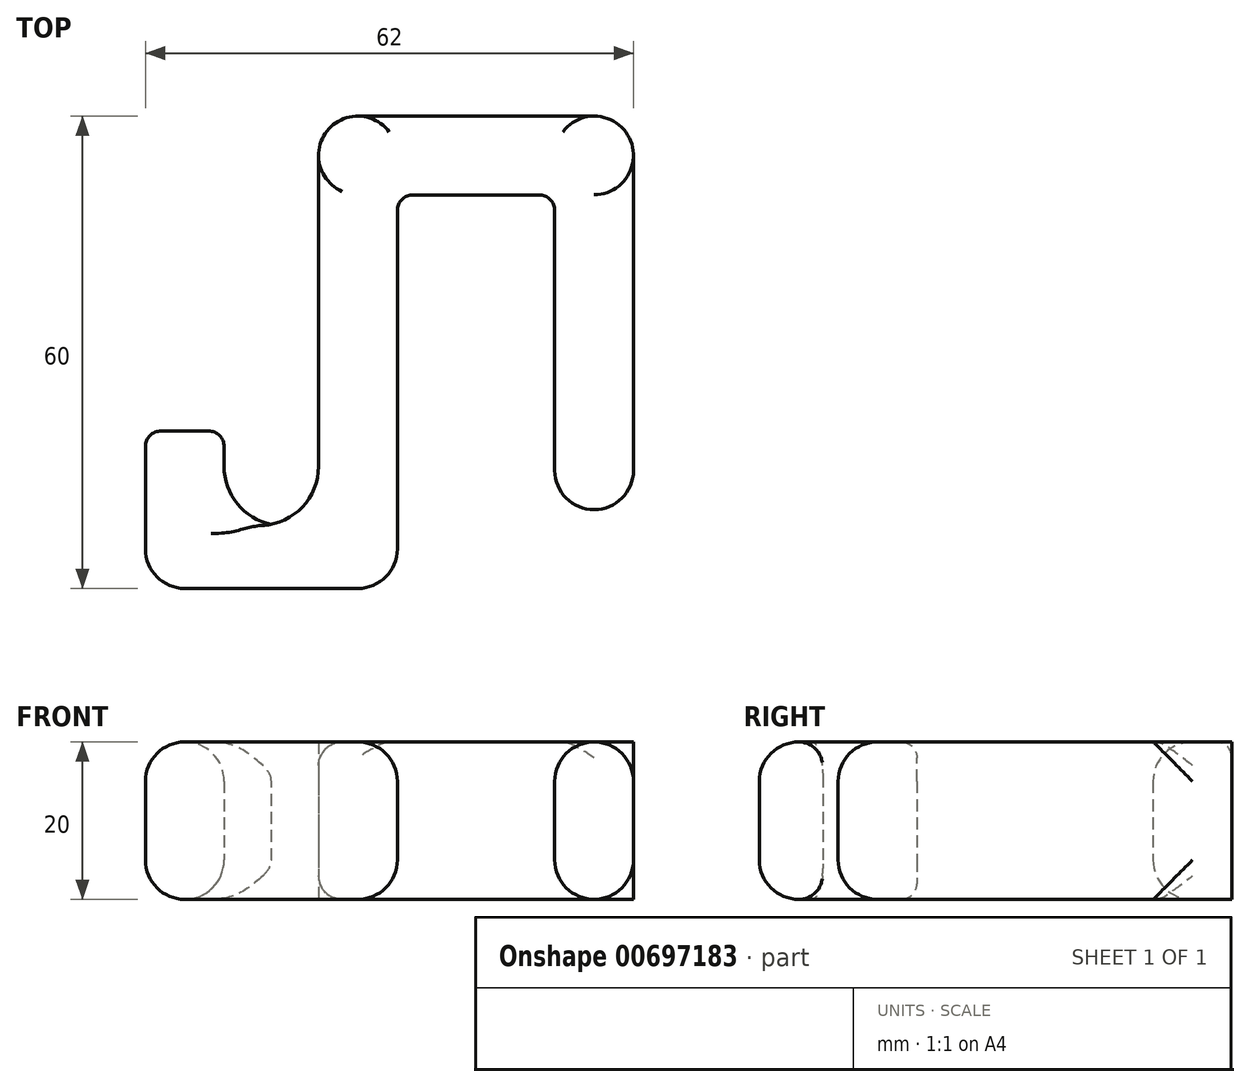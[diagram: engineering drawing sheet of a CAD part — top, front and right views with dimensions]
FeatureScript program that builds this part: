
annotation { "Feature Type Name" : "Feature", "Feature Type Description" : "" }
export const myFeature = defineFeature(function(context is Context, id is Id, definition is map)
    precondition{}
    {
        {
            var Q0;
            Q0=qCreatedBy(makeId("Top.planeOp"),FACE);
            var sketch = newSketch(context, id + "F0", { "sketchPlane" : qUnion([Q0])});
            skLineSegment(sketch, "E0.bottom", {"start": v(10, -20) * mm, "end": v(-10, -20) * mm});
            skLineSegment(sketch, "E0.top", {"start": v(10, 20) * mm, "end": v(-10, 20) * mm});
            skLineSegment(sketch, "E0.left", {"start": v(10, -20) * mm, "end": v(10, 20) * mm});
            skLineSegment(sketch, "E0.right", {"start": v(-10, -20) * mm, "end": v(-10, 20) * mm});
            skPoint(sketch, "E0.middle", {"position": v(0, 0) * mm});
            skLineSegment(sketch, "E1.0", {"start": v(-20, -20) * mm, "end": v(-20, 25) * mm});
            skLineSegment(sketch, "E1.1", {"start": v(15, 30) * mm, "end": v(-15, 30) * mm});
            skLineSegment(sketch, "E1.2", {"start": v(20, -20) * mm, "end": v(20, 25) * mm});
            skLineSegment(sketch, "E2", {"start": v(20, -20) * mm, "end": v(10, -20) * mm});
            skLineSegment(sketch, "E3", {"start": v(-10, -20) * mm, "end": v(-10, -30) * mm});
            skLineSegment(sketch, "E4", {"start": v(-10, -30) * mm, "end": v(-42, -30) * mm});
            skLineSegment(sketch, "E5", {"start": v(-42, -30) * mm, "end": v(-42, -10) * mm});
            skLineSegment(sketch, "E6", {"start": v(-42, -10) * mm, "end": v(-32, -10) * mm});
            skLineSegment(sketch, "E7", {"start": v(-32, -10) * mm, "end": v(-32, -22) * mm});
            skLineSegment(sketch, "E8", {"start": v(-32, -22) * mm, "end": v(-20, -22) * mm});
            skLineSegment(sketch, "E9", {"start": v(-20, -22) * mm, "end": v(-20, -20) * mm});
            skPoint(sketch, "E10.visualSharp", {"position": v(-20, 30) * mm});
            skArc(sketch, "E10.filletArc", {"start": v(-15, 30) * mm, "mid": v(-18.54, 28.54) * mm, "end": v(-20, 25) * mm});
            skPoint(sketch, "E11.visualSharp", {"position": v(20, 30) * mm});
            skArc(sketch, "E11.filletArc", {"start": v(20, 25) * mm, "mid": v(18.54, 28.54) * mm, "end": v(15, 30) * mm});
            skPoint(sketch, "E12.visualSharp", {"position": v(-42, -10) * mm});
            skLineSegment(sketch, "E12.filletArc", {"start": v(-42, -10) * mm, "end": v(-42, -10) * mm});
            skPoint(sketch, "E13.visualSharp", {"position": v(-32, -10) * mm});
            skLineSegment(sketch, "E13.filletArc", {"start": v(-32, -10) * mm, "end": v(-32, -10) * mm});
            skSolve(sketch);
        }
        {
            var Q0;
            Q0=makeQuery(id+"F0.imprint","IMPRINT",FACE,{"disambiguationData":[TD([[makeQuery(id+"F0.imprint","IMPRINT",EDGE,{"derivedFrom":sQuery(id+"F0.wireOp",EDGE,"E0.top")}),-1.0]])]});
            extrude(context, id + "F1", {"entities" : qUnion([Q0]), "depth" : 20 * mm, "offsetDistance" : 25 * mm});
        }
        {
            var Q0;
            Q0=makeQuery(id+"F1.opExtrude","SWEPT_EDGE",EDGE,{"disambiguationData":[OSD([sQuery(id+"F0.wireOp",EDGE,"E8"),sQuery(id+"F0.wireOp",EDGE,"E9")])]});
            var Q1;
            Q1=makeQuery(id+"F1.opExtrude","SWEPT_EDGE",EDGE,{"disambiguationData":[OSD([sQuery(id+"F0.wireOp",EDGE,"E7"),sQuery(id+"F0.wireOp",EDGE,"E8")])]});
            fillet(context, id + "F2", {"entities" : qUnion([Q0, Q1]), "radius" : 7.5 * mm, "tangentPropagation" : true, "allowEdgeOverflow" : false});
        }
        {
            var Q0;
            Q0=makeQuery(id+"F1.opExtrude","SWEPT_EDGE",EDGE,{"disambiguationData":[OSD([sQuery(id+"F0.wireOp",EDGE,"E0.top"),sQuery(id+"F0.wireOp",EDGE,"E0.left")])]});
            var Q1;
            Q1=makeQuery(id+"F1.opExtrude","SWEPT_EDGE",EDGE,{"disambiguationData":[OSD([sQuery(id+"F0.wireOp",EDGE,"E0.top"),sQuery(id+"F0.wireOp",EDGE,"E0.right")])]});
            fillet(context, id + "F3", {"entities" : qUnion([Q0, Q1]), "radius" : 2 * mm, "tangentPropagation" : true, "allowEdgeOverflow" : false});
        }
        {
            var Q0;
            Q0=makeQuery(id+"F1.opExtrude","SWEPT_FACE",FACE,{"disambiguationData":[OSD([sQuery(id+"F0.wireOp",EDGE,"E6")])]});
            var Q1;
            Q1=makeQuery(id+"F1.opExtrude","SWEPT_FACE",FACE,{"disambiguationData":[OSD([sQuery(id+"F0.wireOp",EDGE,"E1.1")])]});
            extrude(context, id + "F4", {"entities" : qUnion([Q0]), "endBound" : BoundingType.UP_TO_SURFACE, "depth" : 25 * mm, "endBoundEntityFace" : qUnion([Q1]), "offsetDistance" : 25 * mm});
        }
        {
            var Q0;
            Q0=makeQuery(id+"F4.opExtrude","SWEPT_FACE",FACE,{"disambiguationData":[OSD([sQuery(id+"F0.wireOp",EDGE,"E5"),sQuery(id+"F0.wireOp",EDGE,"E6")])]});
            var sketch = newSketch(context, id + "F5", { "sketchPlane" : qUnion([Q0])});
            skLineSegment(sketch, "E14.bottom", {"start": v(10, 19) * mm, "end": v(-30, 19) * mm});
            skLineSegment(sketch, "E14.top", {"start": v(10, 18) * mm, "end": v(-30, 18) * mm});
            skLineSegment(sketch, "E14.left", {"start": v(10, 19) * mm, "end": v(10, 18) * mm});
            skLineSegment(sketch, "E14.right", {"start": v(-30, 19) * mm, "end": v(-30, 18) * mm});
            skLineSegment(sketch, "E15.0.1.0", {"start": v(10, 17) * mm, "end": v(-30, 17) * mm});
            skLineSegment(sketch, "E15.0.1.1", {"start": v(10, 16) * mm, "end": v(-30, 16) * mm});
            skLineSegment(sketch, "E15.0.2.0", {"start": v(10, 15) * mm, "end": v(-30, 15) * mm});
            skLineSegment(sketch, "E15.0.2.1", {"start": v(10, 14) * mm, "end": v(-30, 14) * mm});
            skLineSegment(sketch, "E15.0.3.0", {"start": v(10, 13) * mm, "end": v(-30, 13) * mm});
            skLineSegment(sketch, "E15.0.3.1", {"start": v(10, 12) * mm, "end": v(-30, 12) * mm});
            skLineSegment(sketch, "E15.0.4.0", {"start": v(10, 11) * mm, "end": v(-30, 11) * mm});
            skLineSegment(sketch, "E15.0.4.1", {"start": v(10, 10) * mm, "end": v(-30, 10) * mm});
            skLineSegment(sketch, "E15.0.5.0", {"start": v(10, 9) * mm, "end": v(-30, 9) * mm});
            skLineSegment(sketch, "E15.0.5.1", {"start": v(10, 8) * mm, "end": v(-30, 8) * mm});
            skLineSegment(sketch, "E15.0.6.0", {"start": v(10, 7) * mm, "end": v(-30, 7) * mm});
            skLineSegment(sketch, "E15.0.6.1", {"start": v(10, 6) * mm, "end": v(-30, 6) * mm});
            skLineSegment(sketch, "E15.0.7.0", {"start": v(10, 5) * mm, "end": v(-30, 5) * mm});
            skLineSegment(sketch, "E15.0.7.1", {"start": v(10, 4) * mm, "end": v(-30, 4) * mm});
            skLineSegment(sketch, "E15.0.8.0", {"start": v(10, 3) * mm, "end": v(-30, 3) * mm});
            skLineSegment(sketch, "E15.0.8.1", {"start": v(10, 2) * mm, "end": v(-30, 2) * mm});
            skLineSegment(sketch, "E15.0.9.0", {"start": v(10, 1) * mm, "end": v(-30, 1) * mm});
            skLineSegment(sketch, "E15.0.9.1", {"start": v(10, 0) * mm, "end": v(-30, 0) * mm});
            skLineSegment(sketch, "E15.1.0.0", {"start": v(-6, 19) * mm, "end": v(-46, 19) * mm});
            skLineSegment(sketch, "E15.1.0.1", {"start": v(-6, 18) * mm, "end": v(-46, 18) * mm});
            skLineSegment(sketch, "E15.1.1.0", {"start": v(-6, 17) * mm, "end": v(-46, 17) * mm});
            skLineSegment(sketch, "E15.1.1.1", {"start": v(-6, 16) * mm, "end": v(-46, 16) * mm});
            skLineSegment(sketch, "E15.1.2.0", {"start": v(-6, 15) * mm, "end": v(-46, 15) * mm});
            skLineSegment(sketch, "E15.1.2.1", {"start": v(-6, 14) * mm, "end": v(-46, 14) * mm});
            skLineSegment(sketch, "E15.1.3.0", {"start": v(-6, 13) * mm, "end": v(-46, 13) * mm});
            skLineSegment(sketch, "E15.1.3.1", {"start": v(-6, 12) * mm, "end": v(-46, 12) * mm});
            skLineSegment(sketch, "E15.1.4.0", {"start": v(-6, 11) * mm, "end": v(-46, 11) * mm});
            skLineSegment(sketch, "E15.1.4.1", {"start": v(-6, 10) * mm, "end": v(-46, 10) * mm});
            skLineSegment(sketch, "E15.1.5.0", {"start": v(-6, 9) * mm, "end": v(-46, 9) * mm});
            skLineSegment(sketch, "E15.1.5.1", {"start": v(-6, 8) * mm, "end": v(-46, 8) * mm});
            skLineSegment(sketch, "E15.1.6.0", {"start": v(-6, 7) * mm, "end": v(-46, 7) * mm});
            skLineSegment(sketch, "E15.1.6.1", {"start": v(-6, 6) * mm, "end": v(-46, 6) * mm});
            skLineSegment(sketch, "E15.1.7.0", {"start": v(-6, 5) * mm, "end": v(-46, 5) * mm});
            skLineSegment(sketch, "E15.1.7.1", {"start": v(-6, 4) * mm, "end": v(-46, 4) * mm});
            skLineSegment(sketch, "E15.1.8.0", {"start": v(-6, 3) * mm, "end": v(-46, 3) * mm});
            skLineSegment(sketch, "E15.1.8.1", {"start": v(-6, 2) * mm, "end": v(-46, 2) * mm});
            skLineSegment(sketch, "E15.1.9.0", {"start": v(-6, 1) * mm, "end": v(-46, 1) * mm});
            skLineSegment(sketch, "E15.1.9.1", {"start": v(-6, 0) * mm, "end": v(-46, 0) * mm});
            skLineSegment(sketch, "E15.2.0.0", {"start": v(-22, 19) * mm, "end": v(-62, 19) * mm});
            skLineSegment(sketch, "E15.2.0.1", {"start": v(-22, 18) * mm, "end": v(-62, 18) * mm});
            skLineSegment(sketch, "E15.2.1.0", {"start": v(-22, 17) * mm, "end": v(-62, 17) * mm});
            skLineSegment(sketch, "E15.2.1.1", {"start": v(-22, 16) * mm, "end": v(-62, 16) * mm});
            skLineSegment(sketch, "E15.2.2.0", {"start": v(-22, 15) * mm, "end": v(-62, 15) * mm});
            skLineSegment(sketch, "E15.2.2.1", {"start": v(-22, 14) * mm, "end": v(-62, 14) * mm});
            skLineSegment(sketch, "E15.2.3.0", {"start": v(-22, 13) * mm, "end": v(-62, 13) * mm});
            skLineSegment(sketch, "E15.2.3.1", {"start": v(-22, 12) * mm, "end": v(-62, 12) * mm});
            skLineSegment(sketch, "E15.2.4.0", {"start": v(-22, 11) * mm, "end": v(-62, 11) * mm});
            skLineSegment(sketch, "E15.2.4.1", {"start": v(-22, 10) * mm, "end": v(-62, 10) * mm});
            skLineSegment(sketch, "E15.2.5.0", {"start": v(-22, 9) * mm, "end": v(-62, 9) * mm});
            skLineSegment(sketch, "E15.2.5.1", {"start": v(-22, 8) * mm, "end": v(-62, 8) * mm});
            skLineSegment(sketch, "E15.2.6.0", {"start": v(-22, 7) * mm, "end": v(-62, 7) * mm});
            skLineSegment(sketch, "E15.2.6.1", {"start": v(-22, 6) * mm, "end": v(-62, 6) * mm});
            skLineSegment(sketch, "E15.2.7.0", {"start": v(-22, 5) * mm, "end": v(-62, 5) * mm});
            skLineSegment(sketch, "E15.2.7.1", {"start": v(-22, 4) * mm, "end": v(-62, 4) * mm});
            skLineSegment(sketch, "E15.2.8.0", {"start": v(-22, 3) * mm, "end": v(-62, 3) * mm});
            skLineSegment(sketch, "E15.2.8.1", {"start": v(-22, 2) * mm, "end": v(-62, 2) * mm});
            skLineSegment(sketch, "E15.2.9.0", {"start": v(-22, 1) * mm, "end": v(-62, 1) * mm});
            skLineSegment(sketch, "E15.2.9.1", {"start": v(-22, 0) * mm, "end": v(-62, 0) * mm});
            skLineSegment(sketch, "E15.direction1", {"start": v(-30, 19) * mm, "end": v(-46, 19) * mm, "construction": true});
            skLineSegment(sketch, "E15.direction2", {"start": v(-30, 19) * mm, "end": v(-30, 17) * mm, "construction": true});
            skSolve(sketch);
        }
        {
            var Q0;
            {var subQ1=sQuery(id+"F5.wireOp",EDGE,"E14.left");Q0=makeQuery(id+"F5.imprint","IMPRINT",FACE,{"disambiguationData":[TD([[makeQuery(id+"F5.imprint","IMPRINT",EDGE,{"derivedFrom":subQ1}),-1.0]])]});}
            var Q1;
            {var subQ6=sQuery(id+"F5.wireOp",EDGE,"E15.1.1.0");Q1=makeQuery(id+"F5.imprint","IMPRINT",FACE,{"disambiguationData":[TD([[makeQuery(id+"F5.imprint","IMPRINT",EDGE,{"derivedFrom":subQ6}),1.0]])]});}
            var Q2;
            {var subQ6=sQuery(id+"F5.wireOp",EDGE,"E15.1.2.0");Q2=makeQuery(id+"F5.imprint","IMPRINT",FACE,{"disambiguationData":[TD([[makeQuery(id+"F5.imprint","IMPRINT",EDGE,{"derivedFrom":subQ6}),1.0]])]});}
            var Q3;
            {var subQ6=sQuery(id+"F5.wireOp",EDGE,"E15.1.3.0");Q3=makeQuery(id+"F5.imprint","IMPRINT",FACE,{"disambiguationData":[TD([[makeQuery(id+"F5.imprint","IMPRINT",EDGE,{"derivedFrom":subQ6}),1.0]])]});}
            var Q4;
            {var subQ6=sQuery(id+"F5.wireOp",EDGE,"E15.1.4.0");Q4=makeQuery(id+"F5.imprint","IMPRINT",FACE,{"disambiguationData":[TD([[makeQuery(id+"F5.imprint","IMPRINT",EDGE,{"derivedFrom":subQ6}),1.0]])]});}
            var Q5;
            {var subQ6=sQuery(id+"F5.wireOp",EDGE,"E15.1.5.0");Q5=makeQuery(id+"F5.imprint","IMPRINT",FACE,{"disambiguationData":[TD([[makeQuery(id+"F5.imprint","IMPRINT",EDGE,{"derivedFrom":subQ6}),1.0]])]});}
            var Q6;
            {var subQ6=sQuery(id+"F5.wireOp",EDGE,"E15.1.6.0");Q6=makeQuery(id+"F5.imprint","IMPRINT",FACE,{"disambiguationData":[TD([[makeQuery(id+"F5.imprint","IMPRINT",EDGE,{"derivedFrom":subQ6}),1.0]])]});}
            var Q7;
            {var subQ6=sQuery(id+"F5.wireOp",EDGE,"E15.1.7.0");Q7=makeQuery(id+"F5.imprint","IMPRINT",FACE,{"disambiguationData":[TD([[makeQuery(id+"F5.imprint","IMPRINT",EDGE,{"derivedFrom":subQ6}),1.0]])]});}
            var Q8;
            {var subQ6=sQuery(id+"F5.wireOp",EDGE,"E15.1.8.0");Q8=makeQuery(id+"F5.imprint","IMPRINT",FACE,{"disambiguationData":[TD([[makeQuery(id+"F5.imprint","IMPRINT",EDGE,{"derivedFrom":subQ6}),1.0]])]});}
            var Q9;
            {var subQ1=sQuery(id+"F5.wireOp",EDGE,"E15.0.9.1");Q9=makeQuery(id+"F5.imprint","IMPRINT",FACE,{"disambiguationData":[TD([[makeQuery(id+"F5.imprint","IMPRINT",EDGE,{"derivedFrom":subQ1}),1.0]])]});}
            extrude(context, id + "F6", {"entities" : qUnion([Q0, Q1, Q2, Q3, Q4, Q5, Q6, Q7, Q8, Q9]), "operationType" : NewBodyOperationType.REMOVE, "oppositeDirection" : true, "depth" : 14.1 * mm, "offsetDistance" : 25 * mm});
        }
        {
            var Q0;
            {var subQ0=sQuery(id+"F0.wireOp",EDGE,"E6");Q0=makeQuery(id+"F4.opExtrude","SWEPT_FACE",FACE,{"disambiguationData":[OSD([subQ0]),TDD([makeQuery(id+"F1.opExtrude","CAP_EDGE",EDGE,{"disambiguationData":[OSD([subQ0])],"isStart":false})])]});}
            var sketch = newSketch(context, id + "F7", { "sketchPlane" : qUnion([Q0])});
            skLineSegment(sketch, "E16.bottom", {"start": v(-32.8, 30) * mm, "end": v(-33.8, 30) * mm});
            skLineSegment(sketch, "E16.top", {"start": v(-32.8, -10) * mm, "end": v(-33.8, -10) * mm});
            skLineSegment(sketch, "E16.left", {"start": v(-32.8, 30) * mm, "end": v(-32.8, -10) * mm});
            skLineSegment(sketch, "E16.right", {"start": v(-33.8, 30) * mm, "end": v(-33.8, -10) * mm});
            skLineSegment(sketch, "E17.1.0.0", {"start": v(-35.8, 30) * mm, "end": v(-35.8, -10) * mm});
            skLineSegment(sketch, "E17.1.0.1", {"start": v(-34.8, 30) * mm, "end": v(-34.8, -10) * mm});
            skLineSegment(sketch, "E17.2.0.0", {"start": v(-37.8, 30) * mm, "end": v(-37.8, -10) * mm});
            skLineSegment(sketch, "E17.2.0.1", {"start": v(-36.8, 30) * mm, "end": v(-36.8, -10) * mm});
            skLineSegment(sketch, "E17.direction1", {"start": v(-33.8, -10) * mm, "end": v(-35.8, -10) * mm, "construction": true});
            skSolve(sketch);
        }
        {
            var Q0;
            Q0=makeQuery(id+"F7.imprint","IMPRINT",FACE,{"disambiguationData":[TD([[makeQuery(id+"F7.imprint","IMPRINT",EDGE,{"derivedFrom":sQuery(id+"F7.wireOp",EDGE,"E16.bottom")}),1.0]])]});
            var Q1;
            {var subQ0=sQuery(id+"F7.wireOp",EDGE,"E17.1.0.0");Q1=makeQuery(id+"F7.imprint","IMPRINT",FACE,{"disambiguationData":[TD([[makeQuery(id+"F7.imprint","IMPRINT",EDGE,{"derivedFrom":subQ0}),1.0]])]});}
            var Q2;
            {var subQ0=sQuery(id+"F7.wireOp",EDGE,"E17.2.0.1");Q2=makeQuery(id+"F7.imprint","IMPRINT",FACE,{"disambiguationData":[TD([[makeQuery(id+"F7.imprint","IMPRINT",EDGE,{"derivedFrom":subQ0}),-1.0]])]});}
            extrude(context, id + "F8", {"entities" : qUnion([Q0, Q1, Q2]), "operationType" : NewBodyOperationType.REMOVE, "oppositeDirection" : true, "depth" : 25 * mm, "offsetDistance" : 25 * mm});
        }
        {
            var Q0;
            Q0=makeQuery(id+"F1.opExtrude","SWEPT_EDGE",EDGE,{"disambiguationData":[OSD([sQuery(id+"F0.wireOp",EDGE,"E4"),sQuery(id+"F0.wireOp",EDGE,"E5")])]});
            var Q1;
            Q1=makeQuery(id+"F1.opExtrude","SWEPT_EDGE",EDGE,{"disambiguationData":[OSD([sQuery(id+"F0.wireOp",EDGE,"E3"),sQuery(id+"F0.wireOp",EDGE,"E4")])]});
            var Q2;
            Q2=makeQuery(id+"F1.opExtrude","SWEPT_EDGE",EDGE,{"disambiguationData":[OSD([sQuery(id+"F0.wireOp",EDGE,"E0.bottom"),sQuery(id+"F0.wireOp",EDGE,"E0.left"),sQuery(id+"F0.wireOp",EDGE,"E2")])]});
            var Q3;
            Q3=makeQuery(id+"F1.opExtrude","SWEPT_EDGE",EDGE,{"disambiguationData":[OSD([sQuery(id+"F0.wireOp",EDGE,"E1.2"),sQuery(id+"F0.wireOp",EDGE,"E2")])]});
            fillet(context, id + "F9", {"entities" : qUnion([Q0, Q1, Q2, Q3]), "radius" : 5 * mm, "tangentPropagation" : true, "allowEdgeOverflow" : false});
        }
        {
            var Q0;
            Q0=makeQuery(id+"F1.opExtrude","CAP_EDGE",EDGE,{"disambiguationData":[OSD([sQuery(id+"F0.wireOp",EDGE,"E4")])],"isStart":true});
            var Q1;
            Q1=makeQuery(id+"F1.opExtrude","CAP_EDGE",EDGE,{"disambiguationData":[OSD([sQuery(id+"F0.wireOp",EDGE,"E4")])],"isStart":false});
            fillet(context, id + "F10", {"entities" : qUnion([Q0, Q1]), "radius" : 5 * mm, "tangentPropagation" : true, "allowEdgeOverflow" : false});
        }
        {
            var Q0;
            {var subQ0=sQuery(id+"F0.wireOp",EDGE,"E9");var subQ1=sQuery(id+"F0.wireOp",EDGE,"E8");Q0=makeQuery(id+"F2.opFillet","BLEND_EDGE",EDGE,{"blendedFrom":[makeQuery(id+"F1.opExtrude","SWEPT_EDGE",EDGE,{"disambiguationData":[OSD([subQ1,subQ0])]}),makeQuery(id+"F1.opExtrude","CAP_FACE",FACE,{"disambiguationData":[OSD([sQuery(id+"F0.wireOp",EDGE,"E0.top"),sQuery(id+"F0.wireOp",EDGE,"E0.left"),sQuery(id+"F0.wireOp",EDGE,"E0.right"),sQuery(id+"F0.wireOp",EDGE,"E1.0"),sQuery(id+"F0.wireOp",EDGE,"E1.1"),sQuery(id+"F0.wireOp",EDGE,"E1.2"),sQuery(id+"F0.wireOp",EDGE,"E2"),sQuery(id+"F0.wireOp",EDGE,"E3"),sQuery(id+"F0.wireOp",EDGE,"E4"),sQuery(id+"F0.wireOp",EDGE,"E5"),sQuery(id+"F0.wireOp",EDGE,"E6"),sQuery(id+"F0.wireOp",EDGE,"E7"),subQ1,subQ0])],"isStart":true})],"blendedInto":[makeQuery(id+"F1.opExtrude","CAP_FACE",FACE,{"disambiguationData":[OSD([sQuery(id+"F0.wireOp",EDGE,"E0.top"),sQuery(id+"F0.wireOp",EDGE,"E0.left"),sQuery(id+"F0.wireOp",EDGE,"E0.right"),sQuery(id+"F0.wireOp",EDGE,"E1.0"),sQuery(id+"F0.wireOp",EDGE,"E1.1"),sQuery(id+"F0.wireOp",EDGE,"E1.2"),sQuery(id+"F0.wireOp",EDGE,"E2"),sQuery(id+"F0.wireOp",EDGE,"E3"),sQuery(id+"F0.wireOp",EDGE,"E4"),sQuery(id+"F0.wireOp",EDGE,"E5"),sQuery(id+"F0.wireOp",EDGE,"E6"),sQuery(id+"F0.wireOp",EDGE,"E7"),subQ1,subQ0])],"isStart":true})]});}
            var Q1;
            {var subQ0=sQuery(id+"F0.wireOp",EDGE,"E9");var subQ1=sQuery(id+"F0.wireOp",EDGE,"E8");Q1=makeQuery(id+"F2.opFillet","BLEND_EDGE",EDGE,{"blendedFrom":[makeQuery(id+"F1.opExtrude","SWEPT_EDGE",EDGE,{"disambiguationData":[OSD([subQ1,subQ0])]}),makeQuery(id+"F1.opExtrude","CAP_FACE",FACE,{"disambiguationData":[OSD([sQuery(id+"F0.wireOp",EDGE,"E0.top"),sQuery(id+"F0.wireOp",EDGE,"E0.left"),sQuery(id+"F0.wireOp",EDGE,"E0.right"),sQuery(id+"F0.wireOp",EDGE,"E1.0"),sQuery(id+"F0.wireOp",EDGE,"E1.1"),sQuery(id+"F0.wireOp",EDGE,"E1.2"),sQuery(id+"F0.wireOp",EDGE,"E2"),sQuery(id+"F0.wireOp",EDGE,"E3"),sQuery(id+"F0.wireOp",EDGE,"E4"),sQuery(id+"F0.wireOp",EDGE,"E5"),sQuery(id+"F0.wireOp",EDGE,"E6"),sQuery(id+"F0.wireOp",EDGE,"E7"),subQ1,subQ0])],"isStart":false})],"blendedInto":[makeQuery(id+"F1.opExtrude","CAP_FACE",FACE,{"disambiguationData":[OSD([sQuery(id+"F0.wireOp",EDGE,"E0.top"),sQuery(id+"F0.wireOp",EDGE,"E0.left"),sQuery(id+"F0.wireOp",EDGE,"E0.right"),sQuery(id+"F0.wireOp",EDGE,"E1.0"),sQuery(id+"F0.wireOp",EDGE,"E1.1"),sQuery(id+"F0.wireOp",EDGE,"E1.2"),sQuery(id+"F0.wireOp",EDGE,"E2"),sQuery(id+"F0.wireOp",EDGE,"E3"),sQuery(id+"F0.wireOp",EDGE,"E4"),sQuery(id+"F0.wireOp",EDGE,"E5"),sQuery(id+"F0.wireOp",EDGE,"E6"),sQuery(id+"F0.wireOp",EDGE,"E7"),subQ1,subQ0])],"isStart":false})]});}
            fillet(context, id + "F11", {"entities" : qUnion([Q0, Q1]), "radius" : 3 * mm, "tangentPropagation" : true, "allowEdgeOverflow" : false});
        }
        {
            var Q0;
            Q0=makeQuery(id+"F1.opExtrude","CAP_EDGE",EDGE,{"disambiguationData":[OSD([sQuery(id+"F0.wireOp",EDGE,"E7")])],"isStart":false});
            var Q1;
            Q1=makeQuery(id+"F1.opExtrude","CAP_EDGE",EDGE,{"disambiguationData":[OSD([sQuery(id+"F0.wireOp",EDGE,"E7")])],"isStart":true});
            fillet(context, id + "F12", {"entities" : qUnion([Q0, Q1]), "radius" : 5 * mm, "tangentPropagation" : true, "allowEdgeOverflow" : false});
        }
        {
            var Q0;
            Q0=makeQuery(id+"F1.opExtrude","CAP_EDGE",EDGE,{"disambiguationData":[OSD([sQuery(id+"F0.wireOp",EDGE,"E1.1")])],"isStart":false});
            fillet(context, id + "F13", {"entities" : qUnion([Q0]), "radius" : 2 * mm, "tangentPropagation" : true, "allowEdgeOverflow" : false});
        }
        {
            var Q0;
            {var subQ0=sQuery(id+"F0.wireOp",EDGE,"E6");Q0=makeQuery(id+"F8.boolean.opBoolean","SPLIT",FACE,{"disambiguationData":[TD([makeQuery(id+"F8.opExtrude","SWEPT_FACE",FACE,{"disambiguationData":[OSD([sQuery(id+"F7.wireOp",EDGE,"E17.2.0.0")])]})])],"derivedFrom":makeQuery(id+"F4.opExtrude","SWEPT_FACE",FACE,{"disambiguationData":[OSD([subQ0]),TDD([makeQuery(id+"F1.opExtrude","CAP_EDGE",EDGE,{"disambiguationData":[OSD([subQ0])],"isStart":false})])]})});}
            var sketch = newSketch(context, id + "F14", { "sketchPlane" : qUnion([Q0])});
            skLineSegment(sketch, "E18.bottom", {"start": v(-39.9, -10) * mm, "end": v(-38.9, -10) * mm});
            skLineSegment(sketch, "E18.top", {"start": v(-39.9, 30) * mm, "end": v(-38.9, 30) * mm});
            skLineSegment(sketch, "E18.left", {"start": v(-39.9, -10) * mm, "end": v(-39.9, 30) * mm});
            skLineSegment(sketch, "E18.right", {"start": v(-38.9, -10) * mm, "end": v(-38.9, 30) * mm});
            skLineSegment(sketch, "E19.bottom", {"start": v(-42, -10) * mm, "end": v(-41, -10) * mm});
            skLineSegment(sketch, "E19.top", {"start": v(-42, 30) * mm, "end": v(-41, 30) * mm});
            skLineSegment(sketch, "E19.left", {"start": v(-42, -10) * mm, "end": v(-42, 30) * mm});
            skLineSegment(sketch, "E19.right", {"start": v(-41, -10) * mm, "end": v(-41, 30) * mm});
            skSolve(sketch);
        }
        {
            var Q0;
            Q0 = qSketchRegion(id + "F14", true);
            extrude(context, id + "F15", {"entities" : qUnion([Q0]), "operationType" : NewBodyOperationType.REMOVE, "oppositeDirection" : true, "depth" : 25 * mm, "offsetDistance" : 25 * mm});
        }
        {
            var Q0;
            Q0=makeQuery(id+"F1.opExtrude","SWEPT_EDGE",EDGE,{"disambiguationData":[OSD([sQuery(id+"F0.wireOp",EDGE,"E5"),sQuery(id+"F0.wireOp",EDGE,"E6")])]});
            fillet(context, id + "F16", {"entities" : qUnion([Q0]), "radius" : 2 * mm, "tangentPropagation" : true, "allowEdgeOverflow" : false});
        }
        {
            var Q0;
            Q0=makeQuery(id+"F8.boolean.opBoolean","SPLIT",BODY,{"disambiguationData":[OD(1.0)],"derivedFrom":makeQuery(id+"F6.boolean.opBoolean","SPLIT",BODY,{"disambiguationData":[OD(0.0)],"derivedFrom":makeQuery(id+"F4.opExtrude","SWEPT_BODY",BODY,{"disambiguationData":[OSD([sQuery(id+"F0.wireOp",EDGE,"E6")])]})})});
            var Q1;
            Q1=makeQuery(id+"F8.boolean.opBoolean","SPLIT",BODY,{"disambiguationData":[OD(1.0)],"derivedFrom":makeQuery(id+"F6.boolean.opBoolean","SPLIT",BODY,{"disambiguationData":[OD(1.0)],"derivedFrom":makeQuery(id+"F4.opExtrude","SWEPT_BODY",BODY,{"disambiguationData":[OSD([sQuery(id+"F0.wireOp",EDGE,"E6")])]})})});
            var Q2;
            Q2=makeQuery(id+"F8.boolean.opBoolean","SPLIT",BODY,{"disambiguationData":[OD(1.0)],"derivedFrom":makeQuery(id+"F6.boolean.opBoolean","SPLIT",BODY,{"disambiguationData":[OD(2.0)],"derivedFrom":makeQuery(id+"F4.opExtrude","SWEPT_BODY",BODY,{"disambiguationData":[OSD([sQuery(id+"F0.wireOp",EDGE,"E6")])]})})});
            var Q3;
            Q3=makeQuery(id+"F8.boolean.opBoolean","SPLIT",BODY,{"disambiguationData":[OD(1.0)],"derivedFrom":makeQuery(id+"F6.boolean.opBoolean","SPLIT",BODY,{"disambiguationData":[OD(3.0)],"derivedFrom":makeQuery(id+"F4.opExtrude","SWEPT_BODY",BODY,{"disambiguationData":[OSD([sQuery(id+"F0.wireOp",EDGE,"E6")])]})})});
            var Q4;
            Q4=makeQuery(id+"F8.boolean.opBoolean","SPLIT",BODY,{"disambiguationData":[OD(1.0)],"derivedFrom":makeQuery(id+"F6.boolean.opBoolean","SPLIT",BODY,{"disambiguationData":[OD(4.0)],"derivedFrom":makeQuery(id+"F4.opExtrude","SWEPT_BODY",BODY,{"disambiguationData":[OSD([sQuery(id+"F0.wireOp",EDGE,"E6")])]})})});
            var Q5;
            Q5=makeQuery(id+"F8.boolean.opBoolean","SPLIT",BODY,{"disambiguationData":[OD(1.0)],"derivedFrom":makeQuery(id+"F6.boolean.opBoolean","SPLIT",BODY,{"disambiguationData":[OD(5.0)],"derivedFrom":makeQuery(id+"F4.opExtrude","SWEPT_BODY",BODY,{"disambiguationData":[OSD([sQuery(id+"F0.wireOp",EDGE,"E6")])]})})});
            var Q6;
            Q6=makeQuery(id+"F8.boolean.opBoolean","SPLIT",BODY,{"disambiguationData":[OD(1.0)],"derivedFrom":makeQuery(id+"F6.boolean.opBoolean","SPLIT",BODY,{"disambiguationData":[OD(6.0)],"derivedFrom":makeQuery(id+"F4.opExtrude","SWEPT_BODY",BODY,{"disambiguationData":[OSD([sQuery(id+"F0.wireOp",EDGE,"E6")])]})})});
            var Q7;
            Q7=makeQuery(id+"F8.boolean.opBoolean","SPLIT",BODY,{"disambiguationData":[OD(1.0)],"derivedFrom":makeQuery(id+"F6.boolean.opBoolean","SPLIT",BODY,{"disambiguationData":[OD(7.0)],"derivedFrom":makeQuery(id+"F4.opExtrude","SWEPT_BODY",BODY,{"disambiguationData":[OSD([sQuery(id+"F0.wireOp",EDGE,"E6")])]})})});
            var Q8;
            Q8=makeQuery(id+"F8.boolean.opBoolean","SPLIT",BODY,{"disambiguationData":[OD(1.0)],"derivedFrom":makeQuery(id+"F6.boolean.opBoolean","SPLIT",BODY,{"disambiguationData":[OD(8.0)],"derivedFrom":makeQuery(id+"F4.opExtrude","SWEPT_BODY",BODY,{"disambiguationData":[OSD([sQuery(id+"F0.wireOp",EDGE,"E6")])]})})});
            var Q9;
            Q9=makeQuery(id+"F8.boolean.opBoolean","SPLIT",BODY,{"disambiguationData":[OD(1.0)],"derivedFrom":makeQuery(id+"F6.boolean.opBoolean","SPLIT",BODY,{"disambiguationData":[OD(9.0)],"derivedFrom":makeQuery(id+"F4.opExtrude","SWEPT_BODY",BODY,{"disambiguationData":[OSD([sQuery(id+"F0.wireOp",EDGE,"E6")])]})})});
            var Q10;
            Q10=makeQuery(id+"F8.boolean.opBoolean","SPLIT",BODY,{"disambiguationData":[OD(2.0)],"derivedFrom":makeQuery(id+"F6.boolean.opBoolean","SPLIT",BODY,{"disambiguationData":[OD(0.0)],"derivedFrom":makeQuery(id+"F4.opExtrude","SWEPT_BODY",BODY,{"disambiguationData":[OSD([sQuery(id+"F0.wireOp",EDGE,"E6")])]})})});
            var Q11;
            Q11=makeQuery(id+"F8.boolean.opBoolean","SPLIT",BODY,{"disambiguationData":[OD(3.0)],"derivedFrom":makeQuery(id+"F6.boolean.opBoolean","SPLIT",BODY,{"disambiguationData":[OD(0.0)],"derivedFrom":makeQuery(id+"F4.opExtrude","SWEPT_BODY",BODY,{"disambiguationData":[OSD([sQuery(id+"F0.wireOp",EDGE,"E6")])]})})});
            var Q12;
            Q12=makeQuery(id+"F8.boolean.opBoolean","SPLIT",BODY,{"disambiguationData":[OD(2.0)],"derivedFrom":makeQuery(id+"F6.boolean.opBoolean","SPLIT",BODY,{"disambiguationData":[OD(1.0)],"derivedFrom":makeQuery(id+"F4.opExtrude","SWEPT_BODY",BODY,{"disambiguationData":[OSD([sQuery(id+"F0.wireOp",EDGE,"E6")])]})})});
            var Q13;
            Q13=makeQuery(id+"F8.boolean.opBoolean","SPLIT",BODY,{"disambiguationData":[OD(3.0)],"derivedFrom":makeQuery(id+"F6.boolean.opBoolean","SPLIT",BODY,{"disambiguationData":[OD(1.0)],"derivedFrom":makeQuery(id+"F4.opExtrude","SWEPT_BODY",BODY,{"disambiguationData":[OSD([sQuery(id+"F0.wireOp",EDGE,"E6")])]})})});
            var Q14;
            Q14=makeQuery(id+"F8.boolean.opBoolean","SPLIT",BODY,{"disambiguationData":[OD(2.0)],"derivedFrom":makeQuery(id+"F6.boolean.opBoolean","SPLIT",BODY,{"disambiguationData":[OD(2.0)],"derivedFrom":makeQuery(id+"F4.opExtrude","SWEPT_BODY",BODY,{"disambiguationData":[OSD([sQuery(id+"F0.wireOp",EDGE,"E6")])]})})});
            var Q15;
            Q15=makeQuery(id+"F8.boolean.opBoolean","SPLIT",BODY,{"disambiguationData":[OD(3.0)],"derivedFrom":makeQuery(id+"F6.boolean.opBoolean","SPLIT",BODY,{"disambiguationData":[OD(2.0)],"derivedFrom":makeQuery(id+"F4.opExtrude","SWEPT_BODY",BODY,{"disambiguationData":[OSD([sQuery(id+"F0.wireOp",EDGE,"E6")])]})})});
            var Q16;
            Q16=makeQuery(id+"F8.boolean.opBoolean","SPLIT",BODY,{"disambiguationData":[OD(2.0)],"derivedFrom":makeQuery(id+"F6.boolean.opBoolean","SPLIT",BODY,{"disambiguationData":[OD(3.0)],"derivedFrom":makeQuery(id+"F4.opExtrude","SWEPT_BODY",BODY,{"disambiguationData":[OSD([sQuery(id+"F0.wireOp",EDGE,"E6")])]})})});
            var Q17;
            Q17=makeQuery(id+"F8.boolean.opBoolean","SPLIT",BODY,{"disambiguationData":[OD(3.0)],"derivedFrom":makeQuery(id+"F6.boolean.opBoolean","SPLIT",BODY,{"disambiguationData":[OD(3.0)],"derivedFrom":makeQuery(id+"F4.opExtrude","SWEPT_BODY",BODY,{"disambiguationData":[OSD([sQuery(id+"F0.wireOp",EDGE,"E6")])]})})});
            var Q18;
            Q18=makeQuery(id+"F8.boolean.opBoolean","SPLIT",BODY,{"disambiguationData":[OD(2.0)],"derivedFrom":makeQuery(id+"F6.boolean.opBoolean","SPLIT",BODY,{"disambiguationData":[OD(4.0)],"derivedFrom":makeQuery(id+"F4.opExtrude","SWEPT_BODY",BODY,{"disambiguationData":[OSD([sQuery(id+"F0.wireOp",EDGE,"E6")])]})})});
            var Q19;
            Q19=makeQuery(id+"F8.boolean.opBoolean","SPLIT",BODY,{"disambiguationData":[OD(3.0)],"derivedFrom":makeQuery(id+"F6.boolean.opBoolean","SPLIT",BODY,{"disambiguationData":[OD(4.0)],"derivedFrom":makeQuery(id+"F4.opExtrude","SWEPT_BODY",BODY,{"disambiguationData":[OSD([sQuery(id+"F0.wireOp",EDGE,"E6")])]})})});
            var Q20;
            Q20=makeQuery(id+"F8.boolean.opBoolean","SPLIT",BODY,{"disambiguationData":[OD(2.0)],"derivedFrom":makeQuery(id+"F6.boolean.opBoolean","SPLIT",BODY,{"disambiguationData":[OD(5.0)],"derivedFrom":makeQuery(id+"F4.opExtrude","SWEPT_BODY",BODY,{"disambiguationData":[OSD([sQuery(id+"F0.wireOp",EDGE,"E6")])]})})});
            var Q21;
            Q21=makeQuery(id+"F8.boolean.opBoolean","SPLIT",BODY,{"disambiguationData":[OD(3.0)],"derivedFrom":makeQuery(id+"F6.boolean.opBoolean","SPLIT",BODY,{"disambiguationData":[OD(5.0)],"derivedFrom":makeQuery(id+"F4.opExtrude","SWEPT_BODY",BODY,{"disambiguationData":[OSD([sQuery(id+"F0.wireOp",EDGE,"E6")])]})})});
            var Q22;
            Q22=makeQuery(id+"F8.boolean.opBoolean","SPLIT",BODY,{"disambiguationData":[OD(2.0)],"derivedFrom":makeQuery(id+"F6.boolean.opBoolean","SPLIT",BODY,{"disambiguationData":[OD(6.0)],"derivedFrom":makeQuery(id+"F4.opExtrude","SWEPT_BODY",BODY,{"disambiguationData":[OSD([sQuery(id+"F0.wireOp",EDGE,"E6")])]})})});
            var Q23;
            Q23=makeQuery(id+"F8.boolean.opBoolean","SPLIT",BODY,{"disambiguationData":[OD(3.0)],"derivedFrom":makeQuery(id+"F6.boolean.opBoolean","SPLIT",BODY,{"disambiguationData":[OD(6.0)],"derivedFrom":makeQuery(id+"F4.opExtrude","SWEPT_BODY",BODY,{"disambiguationData":[OSD([sQuery(id+"F0.wireOp",EDGE,"E6")])]})})});
            var Q24;
            Q24=makeQuery(id+"F8.boolean.opBoolean","SPLIT",BODY,{"disambiguationData":[OD(2.0)],"derivedFrom":makeQuery(id+"F6.boolean.opBoolean","SPLIT",BODY,{"disambiguationData":[OD(7.0)],"derivedFrom":makeQuery(id+"F4.opExtrude","SWEPT_BODY",BODY,{"disambiguationData":[OSD([sQuery(id+"F0.wireOp",EDGE,"E6")])]})})});
            var Q25;
            Q25=makeQuery(id+"F8.boolean.opBoolean","SPLIT",BODY,{"disambiguationData":[OD(3.0)],"derivedFrom":makeQuery(id+"F6.boolean.opBoolean","SPLIT",BODY,{"disambiguationData":[OD(7.0)],"derivedFrom":makeQuery(id+"F4.opExtrude","SWEPT_BODY",BODY,{"disambiguationData":[OSD([sQuery(id+"F0.wireOp",EDGE,"E6")])]})})});
            var Q26;
            Q26=makeQuery(id+"F8.boolean.opBoolean","SPLIT",BODY,{"disambiguationData":[OD(2.0)],"derivedFrom":makeQuery(id+"F6.boolean.opBoolean","SPLIT",BODY,{"disambiguationData":[OD(8.0)],"derivedFrom":makeQuery(id+"F4.opExtrude","SWEPT_BODY",BODY,{"disambiguationData":[OSD([sQuery(id+"F0.wireOp",EDGE,"E6")])]})})});
            var Q27;
            Q27=makeQuery(id+"F8.boolean.opBoolean","SPLIT",BODY,{"disambiguationData":[OD(3.0)],"derivedFrom":makeQuery(id+"F6.boolean.opBoolean","SPLIT",BODY,{"disambiguationData":[OD(8.0)],"derivedFrom":makeQuery(id+"F4.opExtrude","SWEPT_BODY",BODY,{"disambiguationData":[OSD([sQuery(id+"F0.wireOp",EDGE,"E6")])]})})});
            var Q28;
            Q28=makeQuery(id+"F8.boolean.opBoolean","SPLIT",BODY,{"disambiguationData":[OD(2.0)],"derivedFrom":makeQuery(id+"F6.boolean.opBoolean","SPLIT",BODY,{"disambiguationData":[OD(9.0)],"derivedFrom":makeQuery(id+"F4.opExtrude","SWEPT_BODY",BODY,{"disambiguationData":[OSD([sQuery(id+"F0.wireOp",EDGE,"E6")])]})})});
            var Q29;
            Q29=makeQuery(id+"F8.boolean.opBoolean","SPLIT",BODY,{"disambiguationData":[OD(3.0)],"derivedFrom":makeQuery(id+"F6.boolean.opBoolean","SPLIT",BODY,{"disambiguationData":[OD(9.0)],"derivedFrom":makeQuery(id+"F4.opExtrude","SWEPT_BODY",BODY,{"disambiguationData":[OSD([sQuery(id+"F0.wireOp",EDGE,"E6")])]})})});
            var Q30;
            Q30=makeQuery(id+"F15.boolean.opBoolean","SPLIT",BODY,{"disambiguationData":[OD(0.0)],"derivedFrom":makeQuery(id+"F8.boolean.opBoolean","SPLIT",BODY,{"disambiguationData":[OD(0.0)],"derivedFrom":makeQuery(id+"F6.boolean.opBoolean","SPLIT",BODY,{"disambiguationData":[OD(0.0)],"derivedFrom":makeQuery(id+"F4.opExtrude","SWEPT_BODY",BODY,{"disambiguationData":[OSD([sQuery(id+"F0.wireOp",EDGE,"E6")])]})})})});
            var Q31;
            Q31=makeQuery(id+"F15.boolean.opBoolean","SPLIT",BODY,{"disambiguationData":[OD(1.0)],"derivedFrom":makeQuery(id+"F8.boolean.opBoolean","SPLIT",BODY,{"disambiguationData":[OD(0.0)],"derivedFrom":makeQuery(id+"F6.boolean.opBoolean","SPLIT",BODY,{"disambiguationData":[OD(0.0)],"derivedFrom":makeQuery(id+"F4.opExtrude","SWEPT_BODY",BODY,{"disambiguationData":[OSD([sQuery(id+"F0.wireOp",EDGE,"E6")])]})})})});
            var Q32;
            Q32=makeQuery(id+"F15.boolean.opBoolean","SPLIT",BODY,{"disambiguationData":[OD(0.0)],"derivedFrom":makeQuery(id+"F8.boolean.opBoolean","SPLIT",BODY,{"disambiguationData":[OD(0.0)],"derivedFrom":makeQuery(id+"F6.boolean.opBoolean","SPLIT",BODY,{"disambiguationData":[OD(1.0)],"derivedFrom":makeQuery(id+"F4.opExtrude","SWEPT_BODY",BODY,{"disambiguationData":[OSD([sQuery(id+"F0.wireOp",EDGE,"E6")])]})})})});
            var Q33;
            Q33=makeQuery(id+"F15.boolean.opBoolean","SPLIT",BODY,{"disambiguationData":[OD(1.0)],"derivedFrom":makeQuery(id+"F8.boolean.opBoolean","SPLIT",BODY,{"disambiguationData":[OD(0.0)],"derivedFrom":makeQuery(id+"F6.boolean.opBoolean","SPLIT",BODY,{"disambiguationData":[OD(1.0)],"derivedFrom":makeQuery(id+"F4.opExtrude","SWEPT_BODY",BODY,{"disambiguationData":[OSD([sQuery(id+"F0.wireOp",EDGE,"E6")])]})})})});
            var Q34;
            Q34=makeQuery(id+"F15.boolean.opBoolean","SPLIT",BODY,{"disambiguationData":[OD(0.0)],"derivedFrom":makeQuery(id+"F8.boolean.opBoolean","SPLIT",BODY,{"disambiguationData":[OD(0.0)],"derivedFrom":makeQuery(id+"F6.boolean.opBoolean","SPLIT",BODY,{"disambiguationData":[OD(2.0)],"derivedFrom":makeQuery(id+"F4.opExtrude","SWEPT_BODY",BODY,{"disambiguationData":[OSD([sQuery(id+"F0.wireOp",EDGE,"E6")])]})})})});
            var Q35;
            Q35=makeQuery(id+"F15.boolean.opBoolean","SPLIT",BODY,{"disambiguationData":[OD(1.0)],"derivedFrom":makeQuery(id+"F8.boolean.opBoolean","SPLIT",BODY,{"disambiguationData":[OD(0.0)],"derivedFrom":makeQuery(id+"F6.boolean.opBoolean","SPLIT",BODY,{"disambiguationData":[OD(2.0)],"derivedFrom":makeQuery(id+"F4.opExtrude","SWEPT_BODY",BODY,{"disambiguationData":[OSD([sQuery(id+"F0.wireOp",EDGE,"E6")])]})})})});
            var Q36;
            Q36=makeQuery(id+"F15.boolean.opBoolean","SPLIT",BODY,{"disambiguationData":[OD(0.0)],"derivedFrom":makeQuery(id+"F8.boolean.opBoolean","SPLIT",BODY,{"disambiguationData":[OD(0.0)],"derivedFrom":makeQuery(id+"F6.boolean.opBoolean","SPLIT",BODY,{"disambiguationData":[OD(3.0)],"derivedFrom":makeQuery(id+"F4.opExtrude","SWEPT_BODY",BODY,{"disambiguationData":[OSD([sQuery(id+"F0.wireOp",EDGE,"E6")])]})})})});
            var Q37;
            Q37=makeQuery(id+"F15.boolean.opBoolean","SPLIT",BODY,{"disambiguationData":[OD(1.0)],"derivedFrom":makeQuery(id+"F8.boolean.opBoolean","SPLIT",BODY,{"disambiguationData":[OD(0.0)],"derivedFrom":makeQuery(id+"F6.boolean.opBoolean","SPLIT",BODY,{"disambiguationData":[OD(3.0)],"derivedFrom":makeQuery(id+"F4.opExtrude","SWEPT_BODY",BODY,{"disambiguationData":[OSD([sQuery(id+"F0.wireOp",EDGE,"E6")])]})})})});
            var Q38;
            Q38=makeQuery(id+"F15.boolean.opBoolean","SPLIT",BODY,{"disambiguationData":[OD(0.0)],"derivedFrom":makeQuery(id+"F8.boolean.opBoolean","SPLIT",BODY,{"disambiguationData":[OD(0.0)],"derivedFrom":makeQuery(id+"F6.boolean.opBoolean","SPLIT",BODY,{"disambiguationData":[OD(4.0)],"derivedFrom":makeQuery(id+"F4.opExtrude","SWEPT_BODY",BODY,{"disambiguationData":[OSD([sQuery(id+"F0.wireOp",EDGE,"E6")])]})})})});
            var Q39;
            Q39=makeQuery(id+"F15.boolean.opBoolean","SPLIT",BODY,{"disambiguationData":[OD(1.0)],"derivedFrom":makeQuery(id+"F8.boolean.opBoolean","SPLIT",BODY,{"disambiguationData":[OD(0.0)],"derivedFrom":makeQuery(id+"F6.boolean.opBoolean","SPLIT",BODY,{"disambiguationData":[OD(4.0)],"derivedFrom":makeQuery(id+"F4.opExtrude","SWEPT_BODY",BODY,{"disambiguationData":[OSD([sQuery(id+"F0.wireOp",EDGE,"E6")])]})})})});
            var Q40;
            Q40=makeQuery(id+"F15.boolean.opBoolean","SPLIT",BODY,{"disambiguationData":[OD(0.0)],"derivedFrom":makeQuery(id+"F8.boolean.opBoolean","SPLIT",BODY,{"disambiguationData":[OD(0.0)],"derivedFrom":makeQuery(id+"F6.boolean.opBoolean","SPLIT",BODY,{"disambiguationData":[OD(5.0)],"derivedFrom":makeQuery(id+"F4.opExtrude","SWEPT_BODY",BODY,{"disambiguationData":[OSD([sQuery(id+"F0.wireOp",EDGE,"E6")])]})})})});
            var Q41;
            Q41=makeQuery(id+"F15.boolean.opBoolean","SPLIT",BODY,{"disambiguationData":[OD(1.0)],"derivedFrom":makeQuery(id+"F8.boolean.opBoolean","SPLIT",BODY,{"disambiguationData":[OD(0.0)],"derivedFrom":makeQuery(id+"F6.boolean.opBoolean","SPLIT",BODY,{"disambiguationData":[OD(5.0)],"derivedFrom":makeQuery(id+"F4.opExtrude","SWEPT_BODY",BODY,{"disambiguationData":[OSD([sQuery(id+"F0.wireOp",EDGE,"E6")])]})})})});
            var Q42;
            Q42=makeQuery(id+"F15.boolean.opBoolean","SPLIT",BODY,{"disambiguationData":[OD(0.0)],"derivedFrom":makeQuery(id+"F8.boolean.opBoolean","SPLIT",BODY,{"disambiguationData":[OD(0.0)],"derivedFrom":makeQuery(id+"F6.boolean.opBoolean","SPLIT",BODY,{"disambiguationData":[OD(6.0)],"derivedFrom":makeQuery(id+"F4.opExtrude","SWEPT_BODY",BODY,{"disambiguationData":[OSD([sQuery(id+"F0.wireOp",EDGE,"E6")])]})})})});
            var Q43;
            Q43=makeQuery(id+"F15.boolean.opBoolean","SPLIT",BODY,{"disambiguationData":[OD(1.0)],"derivedFrom":makeQuery(id+"F8.boolean.opBoolean","SPLIT",BODY,{"disambiguationData":[OD(0.0)],"derivedFrom":makeQuery(id+"F6.boolean.opBoolean","SPLIT",BODY,{"disambiguationData":[OD(6.0)],"derivedFrom":makeQuery(id+"F4.opExtrude","SWEPT_BODY",BODY,{"disambiguationData":[OSD([sQuery(id+"F0.wireOp",EDGE,"E6")])]})})})});
            var Q44;
            Q44=makeQuery(id+"F15.boolean.opBoolean","SPLIT",BODY,{"disambiguationData":[OD(0.0)],"derivedFrom":makeQuery(id+"F8.boolean.opBoolean","SPLIT",BODY,{"disambiguationData":[OD(0.0)],"derivedFrom":makeQuery(id+"F6.boolean.opBoolean","SPLIT",BODY,{"disambiguationData":[OD(7.0)],"derivedFrom":makeQuery(id+"F4.opExtrude","SWEPT_BODY",BODY,{"disambiguationData":[OSD([sQuery(id+"F0.wireOp",EDGE,"E6")])]})})})});
            var Q45;
            Q45=makeQuery(id+"F15.boolean.opBoolean","SPLIT",BODY,{"disambiguationData":[OD(1.0)],"derivedFrom":makeQuery(id+"F8.boolean.opBoolean","SPLIT",BODY,{"disambiguationData":[OD(0.0)],"derivedFrom":makeQuery(id+"F6.boolean.opBoolean","SPLIT",BODY,{"disambiguationData":[OD(7.0)],"derivedFrom":makeQuery(id+"F4.opExtrude","SWEPT_BODY",BODY,{"disambiguationData":[OSD([sQuery(id+"F0.wireOp",EDGE,"E6")])]})})})});
            var Q46;
            Q46=makeQuery(id+"F15.boolean.opBoolean","SPLIT",BODY,{"disambiguationData":[OD(0.0)],"derivedFrom":makeQuery(id+"F8.boolean.opBoolean","SPLIT",BODY,{"disambiguationData":[OD(0.0)],"derivedFrom":makeQuery(id+"F6.boolean.opBoolean","SPLIT",BODY,{"disambiguationData":[OD(8.0)],"derivedFrom":makeQuery(id+"F4.opExtrude","SWEPT_BODY",BODY,{"disambiguationData":[OSD([sQuery(id+"F0.wireOp",EDGE,"E6")])]})})})});
            var Q47;
            Q47=makeQuery(id+"F15.boolean.opBoolean","SPLIT",BODY,{"disambiguationData":[OD(1.0)],"derivedFrom":makeQuery(id+"F8.boolean.opBoolean","SPLIT",BODY,{"disambiguationData":[OD(0.0)],"derivedFrom":makeQuery(id+"F6.boolean.opBoolean","SPLIT",BODY,{"disambiguationData":[OD(8.0)],"derivedFrom":makeQuery(id+"F4.opExtrude","SWEPT_BODY",BODY,{"disambiguationData":[OSD([sQuery(id+"F0.wireOp",EDGE,"E6")])]})})})});
            var Q48;
            Q48=makeQuery(id+"F15.boolean.opBoolean","SPLIT",BODY,{"disambiguationData":[OD(0.0)],"derivedFrom":makeQuery(id+"F8.boolean.opBoolean","SPLIT",BODY,{"disambiguationData":[OD(0.0)],"derivedFrom":makeQuery(id+"F6.boolean.opBoolean","SPLIT",BODY,{"disambiguationData":[OD(9.0)],"derivedFrom":makeQuery(id+"F4.opExtrude","SWEPT_BODY",BODY,{"disambiguationData":[OSD([sQuery(id+"F0.wireOp",EDGE,"E6")])]})})})});
            var Q49;
            Q49=makeQuery(id+"F15.boolean.opBoolean","SPLIT",BODY,{"disambiguationData":[OD(1.0)],"derivedFrom":makeQuery(id+"F8.boolean.opBoolean","SPLIT",BODY,{"disambiguationData":[OD(0.0)],"derivedFrom":makeQuery(id+"F6.boolean.opBoolean","SPLIT",BODY,{"disambiguationData":[OD(9.0)],"derivedFrom":makeQuery(id+"F4.opExtrude","SWEPT_BODY",BODY,{"disambiguationData":[OSD([sQuery(id+"F0.wireOp",EDGE,"E6")])]})})})});
            deleteBodies(context, id + "F17", {"entities" : qUnion([Q0, Q1, Q2, Q3, Q4, Q5, Q6, Q7, Q8, Q9, Q10, Q11, Q12, Q13, Q14, Q15, Q16, Q17, Q18, Q19, Q20, Q21, Q22, Q23, Q24, Q25, Q26, Q27, Q28, Q29, Q30, Q31, Q32, Q33, Q34, Q35, Q36, Q37, Q38, Q39, Q40, Q41, Q42, Q43, Q44, Q45, Q46, Q47, Q48, Q49])});
        }
    });
